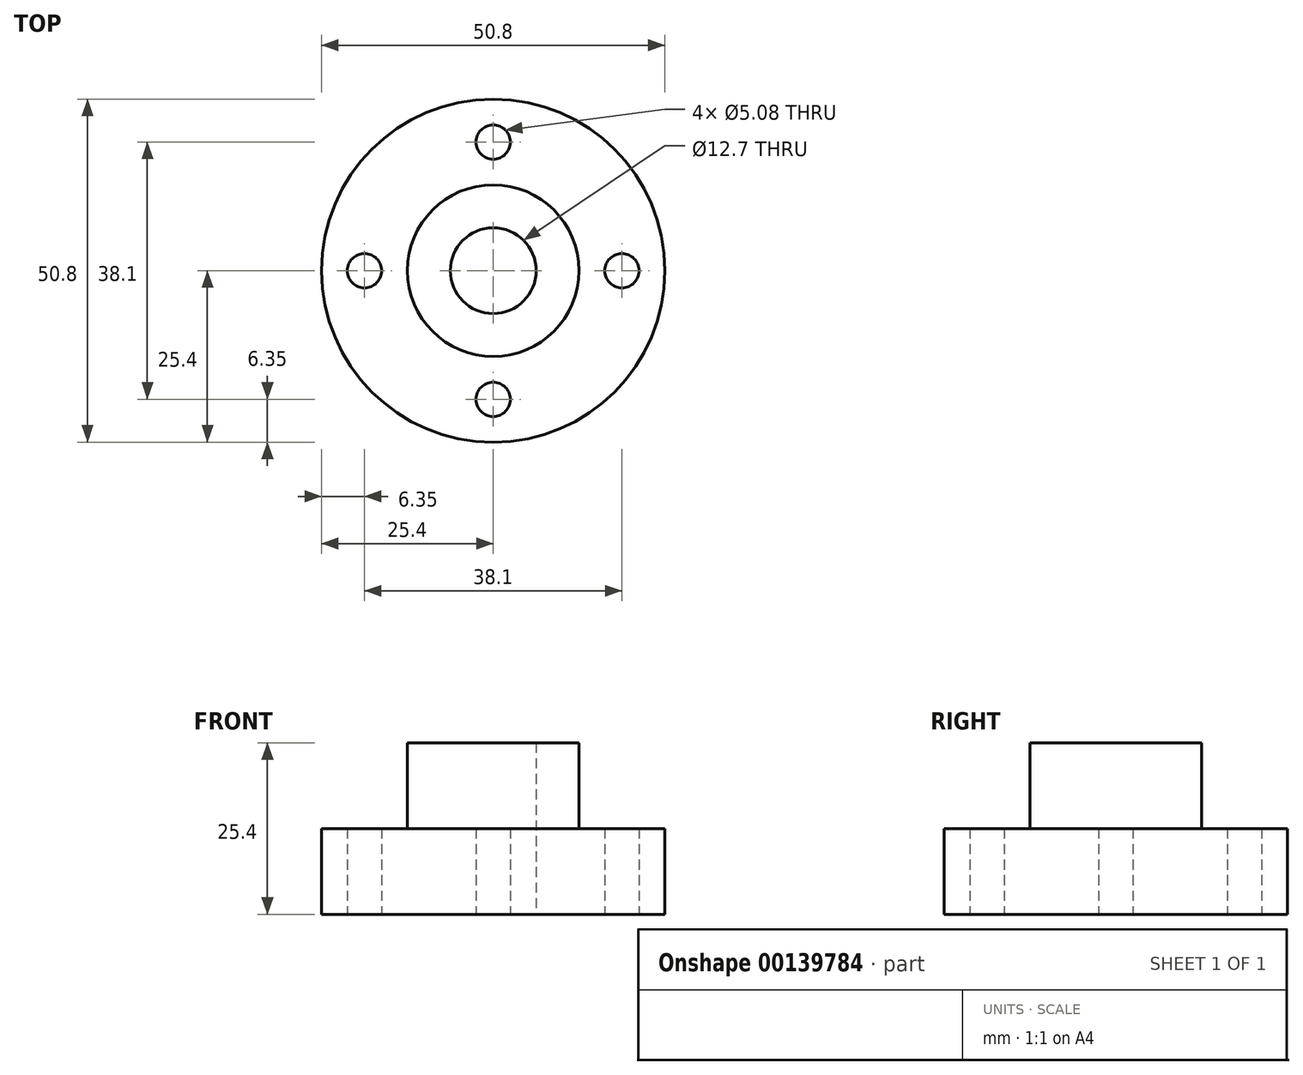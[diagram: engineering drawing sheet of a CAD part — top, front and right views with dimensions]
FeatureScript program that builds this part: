
annotation { "Feature Type Name" : "Feature", "Feature Type Description" : "" }
export const myFeature = defineFeature(function(context is Context, id is Id, definition is map)
    precondition{}
    {
        {
            var Q0;
            Q0=qCreatedBy(makeId("Top.planeOp"),FACE);
            var sketch = newSketch(context, id + "F0", { "sketchPlane" : qUnion([Q0])});
            skCircle(sketch, "E0", {"center": v(0, 0) * mm, "radius": 25.4 * mm});
            skSolve(sketch);
        }
        {
            var Q0;
            Q0 = qSketchRegion(id + "F0", true);
            extrude(context, id + "F1", {"entities" : qUnion([Q0]), "depth" : 12.7 * mm});
        }
        {
            var Q0;
            Q0=qCreatedBy(makeId("Top.planeOp"),FACE);
            var sketch = newSketch(context, id + "F2", { "sketchPlane" : qUnion([Q0])});
            skCircle(sketch, "E1", {"center": v(0, 0) * mm, "radius": 12.7 * mm});
            skSolve(sketch);
        }
        {
            var Q0;
            Q0 = qSketchRegion(id + "F2", true);
            extrude(context, id + "F3", {"entities" : qUnion([Q0]), "operationType" : NewBodyOperationType.ADD, "depth" : 25.4 * mm});
        }
        {
            var Q0;
            Q0=qCreatedBy(makeId("Top.planeOp"),FACE);
            var sketch = newSketch(context, id + "F4", { "sketchPlane" : qUnion([Q0])});
            skCircle(sketch, "E2", {"center": v(0, 0) * mm, "radius": 19.05 * mm, "construction": true});
            skCircle(sketch, "E3", {"center": v(0, 19.05) * mm, "radius": 2.54 * mm});
            skCircle(sketch, "E4.1.0", {"center": v(-19.05, 0) * mm, "radius": 2.54 * mm});
            skCircle(sketch, "E4.2.0", {"center": v(0, -19.05) * mm, "radius": 2.54 * mm});
            skCircle(sketch, "E4.3.0", {"center": v(19.05, 0) * mm, "radius": 2.54 * mm});
            skCircle(sketch, "E5", {"center": v(0, 0) * mm, "radius": 6.35 * mm});
            skSolve(sketch);
        }
        {
            var Q0;
            Q0 = qSketchRegion(id + "F4", true);
            extrude(context, id + "F5", {"entities" : qUnion([Q0]), "operationType" : NewBodyOperationType.REMOVE, "depth" : 25.4 * mm});
        }
    });
